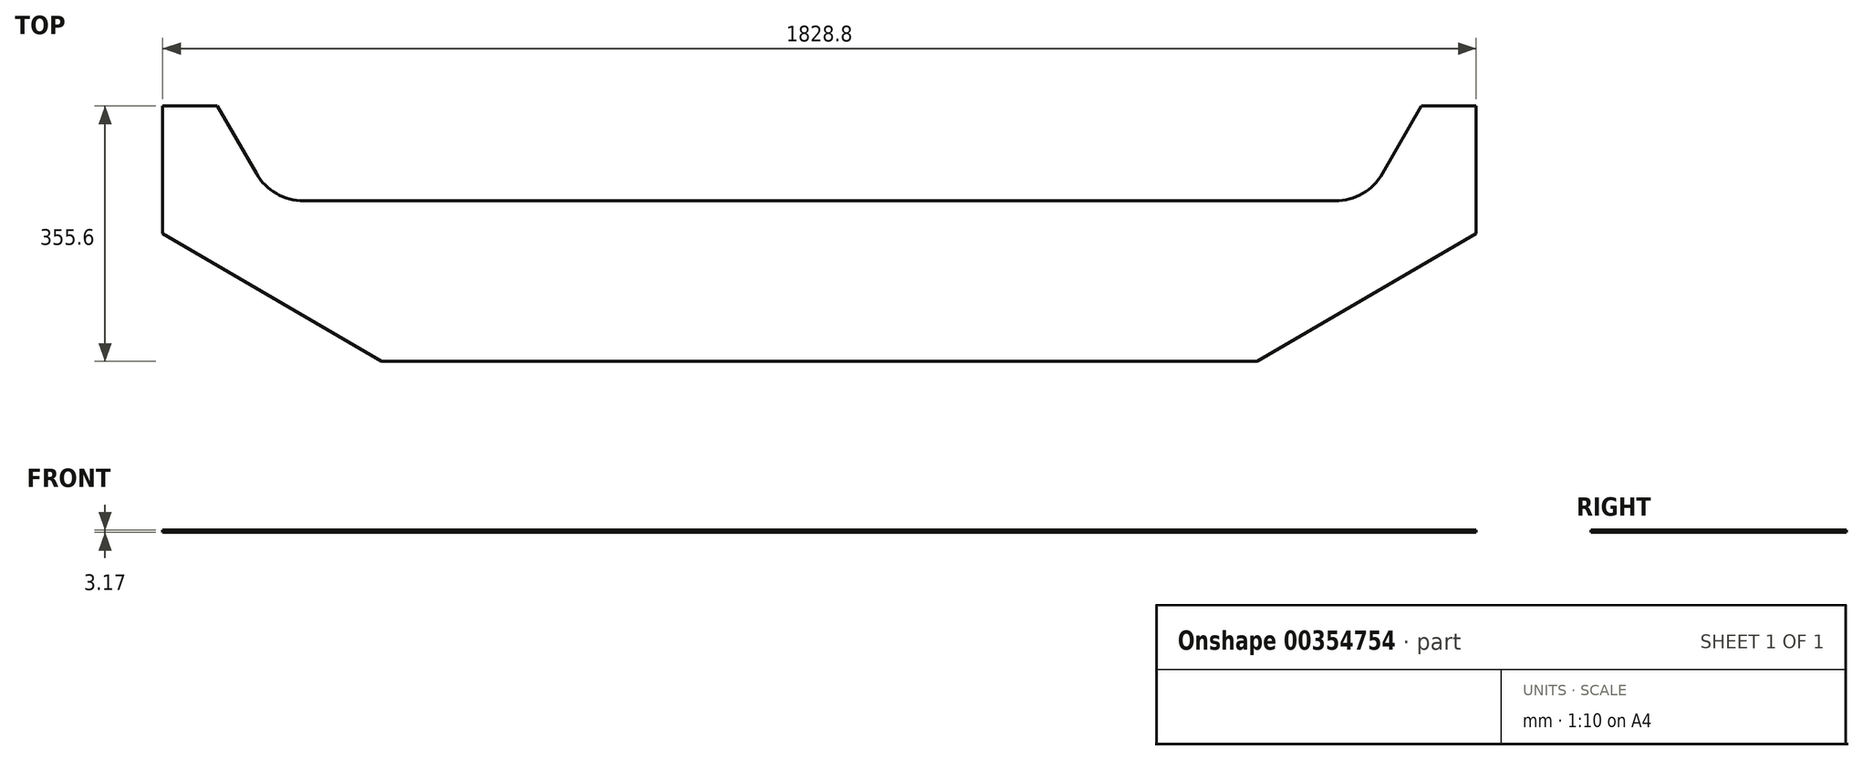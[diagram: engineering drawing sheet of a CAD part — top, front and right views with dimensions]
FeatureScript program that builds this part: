
annotation { "Feature Type Name" : "Feature", "Feature Type Description" : "" }
export const myFeature = defineFeature(function(context is Context, id is Id, definition is map)
    precondition{}
    {
        {
            var Q0;
            Q0=qCreatedBy(makeId("Top.planeOp"),FACE);
            var sketch = newSketch(context, id + "F0", { "sketchPlane" : qUnion([Q0])});
            skLineSegment(sketch, "E0.bottom", {"start": v(914.4, 131.98) * mm, "end": v(838.2, 131.98) * mm});
            skLineSegment(sketch, "E0.top", {"start": v(609.6, -223.62) * mm, "end": v(-609.6, -223.62) * mm});
            skLineSegment(sketch, "E0.left", {"start": v(914.4, 131.98) * mm, "end": v(914.4, -45.82) * mm});
            skLineSegment(sketch, "E0.right", {"start": v(-914.4, 131.98) * mm, "end": v(-914.4, -45.82) * mm});
            skPoint(sketch, "E0.middle", {"position": v(0, -45.82) * mm});
            skLineSegment(sketch, "E1", {"start": v(-914.4, -45.82) * mm, "end": v(-609.6, -223.62) * mm});
            skLineSegment(sketch, "E2", {"start": v(914.4, -45.82) * mm, "end": v(609.6, -223.62) * mm});
            skLineSegment(sketch, "E3", {"start": v(-838.2, 131.98) * mm, "end": v(-784, 38.1) * mm});
            skLineSegment(sketch, "E4", {"start": v(-718, 0) * mm, "end": v(718, 0) * mm});
            skLineSegment(sketch, "E5", {"start": v(784, 38.1) * mm, "end": v(838.2, 131.98) * mm});
            skLineSegment(sketch, "E6.trimOffspring", {"start": v(-838.2, 131.98) * mm, "end": v(-914.4, 131.98) * mm});
            skPoint(sketch, "E7.orphan", {"position": v(-914.4, -223.62) * mm});
            skPoint(sketch, "E8.orphan", {"position": v(914.4, -223.62) * mm});
            skPoint(sketch, "E9.visualSharp", {"position": v(-762, 0) * mm});
            skArc(sketch, "E9.filletArc", {"start": v(-784, 38.1) * mm, "mid": v(-756.1, 10.2) * mm, "end": v(-718, 0) * mm});
            skPoint(sketch, "E10.visualSharp", {"position": v(762, 0) * mm});
            skArc(sketch, "E10.filletArc", {"start": v(718, 0) * mm, "mid": v(756.1, 10.2) * mm, "end": v(784, 38.1) * mm});
            skSolve(sketch);
        }
        {
            var Q0;
            Q0=makeQuery(id+"F0.imprint","IMPRINT",FACE,{"disambiguationData":[TD([[makeQuery(id+"F0.imprint","IMPRINT",EDGE,{"derivedFrom":sQuery(id+"F0.wireOp",EDGE,"E0.bottom")}),1.0]])]});
            extrude(context, id + "F1", {"entities" : qUnion([Q0]), "depth" : 3.17 * mm});
        }
    });
